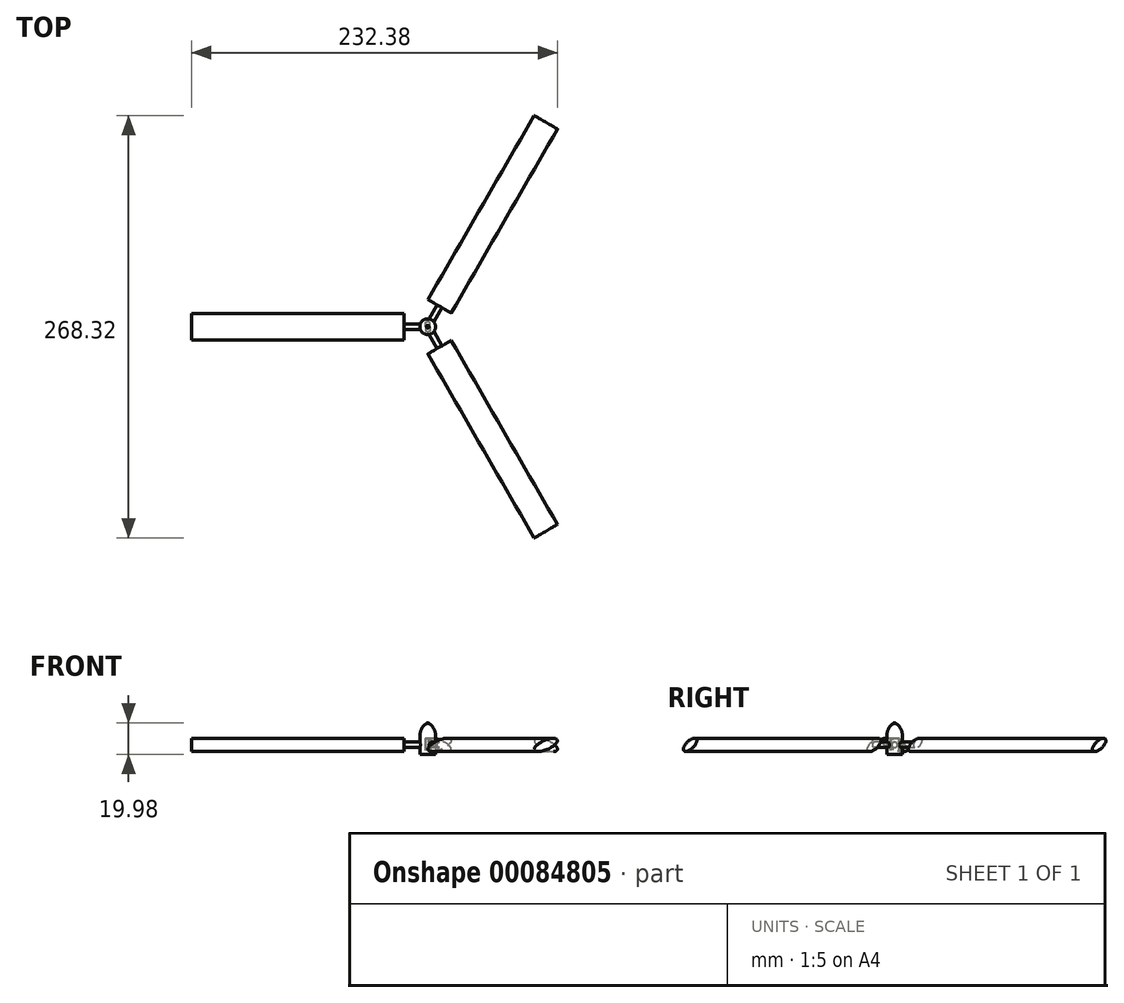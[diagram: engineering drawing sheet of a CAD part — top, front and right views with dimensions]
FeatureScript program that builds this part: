
annotation { "Feature Type Name" : "Feature", "Feature Type Description" : "" }
export const myFeature = defineFeature(function(context is Context, id is Id, definition is map)
    precondition{}
    {
        {
            var Q0;
            Q0=qCreatedBy(makeId("Right.planeOp"),FACE);
            var sketch = newSketch(context, id + "F0", { "sketchPlane" : qUnion([Q0])});
            skLineSegment(sketch, "E0", {"start": v(0, 0) * mm, "end": v(0, 20) * mm, "construction": true});
            skLineSegment(sketch, "E1", {"start": v(0, 0) * mm, "end": v(5, 0) * mm});
            skLineSegment(sketch, "E2", {"start": v(5, 0) * mm, "end": v(5, 11.6) * mm});
            skArc(sketch, "E3.filletArc", {"start": v(5, 11.6) * mm, "mid": v(3.92, 16.13) * mm, "end": v(0.9, 19.67) * mm});
            skArc(sketch, "E4", {"start": v(0.9, 19.67) * mm, "mid": v(0.48, 19.9) * mm, "end": v(0, 19.98) * mm});
            skLineSegment(sketch, "E5", {"start": v(0, 19.98) * mm, "end": v(0, 0) * mm});
            skSolve(sketch);
        }
        {
            var Q0;
            Q0 = qSketchRegion(id + "F0", true);
            var Q1;
            Q1=sQuery(id+"F0.wireOp",EDGE,"E0");
            revolve(context, id + "F1", {"entities" : qUnion([Q0]), "axis" : qUnion([Q1]), "revolveType" : RevolveType.FULL});
        }
        {
            var Q0;
            Q0=qCreatedBy(makeId("Right.planeOp"),FACE);
            cPlane(context, id + "F2", {"entities" : qUnion([Q0]), "cplaneType" : CPlaneType.OFFSET, "offset" : 150 * mm, "oppositeDirection" : true, "width" : 150 * mm, "height" : 150 * mm});
        }
        {
            var Q0;
            Q0=qCreatedBy(id+"F2.planeOp",FACE);
            var sketch = newSketch(context, id + "F3", { "sketchPlane" : qUnion([Q0])});
            skLineSegment(sketch, "E6", {"start": v(0, 6.03) * mm, "end": v(9.1, 6.03) * mm, "construction": true});
            skLineSegment(sketch, "E7", {"start": v(0, 6.03) * mm, "end": v(8.46, 2.95) * mm, "construction": true});
            skEllipse(sketch, "E8", {"center": v(0, 6.03) * mm, "majorRadius": 9 * mm, "minorRadius": 3.04 * mm, "majorAxis": v(0.94, -0.34)});
            skLineSegment(sketch, "E9", {"start": v(0, 6.03) * mm, "end": v(1.03, 8.84) * mm, "construction": true});
            skSolve(sketch);
        }
        {
            var Q0;
            Q0 = qSketchRegion(id + "F3", true);
            extrude(context, id + "F4", {"entities" : qUnion([Q0]), "depth" : 135 * mm});
        }
        {
            var Q0;
            Q0=makeQuery(id+"F4.opExtrude","CAP_FACE",FACE,{"disambiguationData":[OSD([sQuery(id+"F3.wireOp",EDGE,"E8")])],"isStart":false});
            var sketch = newSketch(context, id + "F5", { "sketchPlane" : qUnion([Q0])});
            skCircle(sketch, "E10", {"center": v(0, 6.03) * mm, "radius": 1.75 * mm});
            skSolve(sketch);
        }
        {
            var Q0;
            Q0 = qSketchRegion(id + "F5", true);
            extrude(context, id + "F6", {"entities" : qUnion([Q0]), "operationType" : NewBodyOperationType.ADD, "depth" : 15 * mm});
        }
        {
            var Q0;
            Q0=makeQuery(id+"F1.opRevolve","SWEPT_BODY",BODY,{"disambiguationData":[OSD([sQuery(id+"F0.wireOp",EDGE,"E1"),sQuery(id+"F0.wireOp",EDGE,"E2"),sQuery(id+"F0.wireOp",EDGE,"E3.filletArc"),sQuery(id+"F0.wireOp",EDGE,"E4"),sQuery(id+"F0.wireOp",EDGE,"E5")])]});
            var Q1;
            Q1=makeQuery(id+"F1.opRevolve","SWEPT_EDGE",EDGE,{"disambiguationData":[OSD([sQuery(id+"F0.wireOp",EDGE,"E1"),sQuery(id+"F0.wireOp",EDGE,"E2")])]});
            circularPattern(context, id + "F7", {"operationType" : NewBodyOperationType.ADD, "entities" : qUnion([Q0]), "axis" : qUnion([Q1]), "angle" : 120 * degree, "instanceCount" : 3});
        }
        {
            var Q0;
            Q0=makeQuery(id+"F1.opRevolve","SWEPT_FACE",FACE,{"disambiguationData":[OSD([sQuery(id+"F0.wireOp",EDGE,"E1")])]});
            var sketch = newSketch(context, id + "F8", { "sketchPlane" : qUnion([Q0])});
            skPoint(sketch, "E11.middle", {"position": v(0, 0) * mm});
            skLineSegment(sketch, "E12", {"start": v(0, -2.96) * mm, "end": v(0, 0) * mm, "construction": true});
            skPoint(sketch, "E13.orphan", {"position": v(-1.64, -2.47) * mm});
            skPoint(sketch, "E14.end.orphan", {"position": v(1.53, -2.53) * mm});
            skPoint(sketch, "E15.orphan", {"position": v(1.64, 2.47) * mm});
            skPoint(sketch, "E16.start.orphan", {"position": v(-1.53, 2.53) * mm});
            skCircle(sketch, "E17", {"center": v(0, 0) * mm, "radius": 3 * mm, "construction": true});
            skLineSegment(sketch, "E18", {"start": v(-1.64, -2.47) * mm, "end": v(-1.53, 2.53) * mm});
            skLineSegment(sketch, "E19", {"start": v(1.64, 2.47) * mm, "end": v(1.53, -2.53) * mm});
            skLineSegment(sketch, "E20", {"start": v(-1.53, 2.53) * mm, "end": v(1.64, 2.47) * mm, "construction": true});
            skLineSegment(sketch, "E21", {"start": v(1.53, -2.53) * mm, "end": v(-1.64, -2.47) * mm, "construction": true});
            skArc(sketch, "E22", {"start": v(1.64, 2.47) * mm, "mid": v(0.06, 2.96) * mm, "end": v(-1.53, 2.53) * mm});
            skArc(sketch, "E23", {"start": v(-1.64, -2.47) * mm, "mid": v(-0.06, -2.96) * mm, "end": v(1.53, -2.53) * mm});
            skSolve(sketch);
        }
        {
            var Q0;
            Q0 = qSketchRegion(id + "F8", true);
            extrude(context, id + "F9", {"entities" : qUnion([Q0]), "operationType" : NewBodyOperationType.REMOVE, "oppositeDirection" : true, "depth" : 10 * mm});
        }
    });
